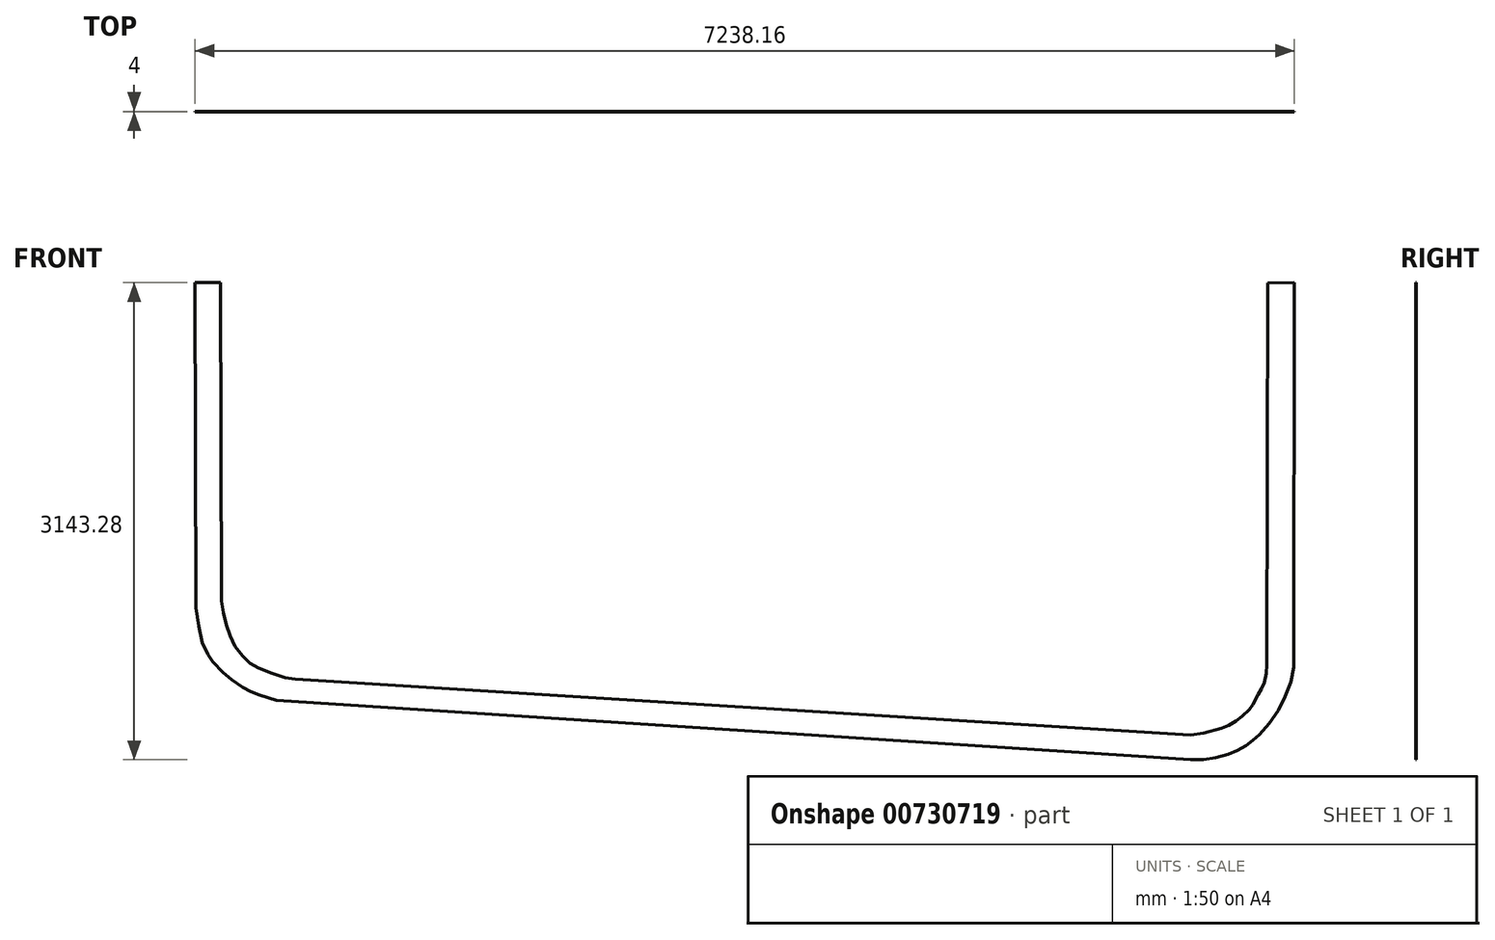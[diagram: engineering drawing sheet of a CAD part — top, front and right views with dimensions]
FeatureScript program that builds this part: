
annotation { "Feature Type Name" : "Feature", "Feature Type Description" : "" }
export const myFeature = defineFeature(function(context is Context, id is Id, definition is map)
    precondition{}
    {
        {
            var Q0;
            Q0=qCreatedBy(makeId("Front.planeOp"),FACE);
            var sketch = newSketch(context, id + "F0", { "sketchPlane" : qUnion([Q0])});
            skLineSegment(sketch, "E0", {"start": v(-3619.08, 1571.64) * mm, "end": v(-3450.88, 1571.64) * mm});
            skLineSegment(sketch, "E1", {"start": v(-3450.88, 1571.64) * mm, "end": v(-3446.72, -525.59) * mm});
            skLineSegment(sketch, "E2", {"start": v(-3446.72, -525.59) * mm, "end": v(-3573.72, -525.84) * mm});
            skLineSegment(sketch, "E3", {"start": v(-3573.72, -525.84) * mm, "end": v(-3446.72, -525.59) * mm});
            skLineSegment(sketch, "E4", {"start": v(-3446.72, -525.59) * mm, "end": v(-3431.83, -603.7) * mm});
            skLineSegment(sketch, "E5", {"start": v(-3431.83, -603.7) * mm, "end": v(-3411.94, -681.16) * mm});
            skLineSegment(sketch, "E6", {"start": v(-3411.94, -681.16) * mm, "end": v(-3389.03, -755.43) * mm});
            skLineSegment(sketch, "E7", {"start": v(-3389.03, -755.43) * mm, "end": v(-3355.94, -824.45) * mm});
            skLineSegment(sketch, "E8", {"start": v(-3355.94, -824.45) * mm, "end": v(-3304.78, -889.17) * mm});
            skLineSegment(sketch, "E9", {"start": v(-3304.78, -889.17) * mm, "end": v(-3259.32, -934.86) * mm});
            skLineSegment(sketch, "E10", {"start": v(-3259.32, -934.86) * mm, "end": v(-3201.02, -968.1) * mm});
            skLineSegment(sketch, "E11", {"start": v(-3201.02, -968.1) * mm, "end": v(-3110.78, -1003.16) * mm});
            skLineSegment(sketch, "E12", {"start": v(-3110.78, -1003.16) * mm, "end": v(-3026.42, -1029.63) * mm});
            skLineSegment(sketch, "E13", {"start": v(-3026.42, -1029.63) * mm, "end": v(-2959.34, -1040.5) * mm});
            skLineSegment(sketch, "E14", {"start": v(-2959.34, -1040.5) * mm, "end": v(-2979.69, -1165.87) * mm});
            skLineSegment(sketch, "E15", {"start": v(-2979.69, -1165.87) * mm, "end": v(-2959.34, -1040.5) * mm});
            skLineSegment(sketch, "E16", {"start": v(-2959.34, -1040.5) * mm, "end": v(2935.08, -1409.53) * mm});
            skLineSegment(sketch, "E17", {"start": v(2935.08, -1409.53) * mm, "end": v(2927.13, -1536.28) * mm});
            skLineSegment(sketch, "E18", {"start": v(2927.13, -1536.28) * mm, "end": v(2935.08, -1409.53) * mm});
            skLineSegment(sketch, "E19", {"start": v(2935.08, -1409.53) * mm, "end": v(3023.48, -1394.9) * mm});
            skLineSegment(sketch, "E20", {"start": v(3023.48, -1394.9) * mm, "end": v(3140.7, -1365.72) * mm});
            skLineSegment(sketch, "E21", {"start": v(3140.7, -1365.72) * mm, "end": v(3188.35, -1344.82) * mm});
            skLineSegment(sketch, "E22", {"start": v(3188.35, -1344.82) * mm, "end": v(3234.63, -1316.42) * mm});
            skLineSegment(sketch, "E23", {"start": v(3234.63, -1316.42) * mm, "end": v(3278.04, -1283.37) * mm});
            skLineSegment(sketch, "E24", {"start": v(3278.04, -1283.37) * mm, "end": v(3323.53, -1240.37) * mm});
            skLineSegment(sketch, "E25", {"start": v(3323.53, -1240.37) * mm, "end": v(3346.54, -1207.58) * mm});
            skLineSegment(sketch, "E26", {"start": v(3346.54, -1207.58) * mm, "end": v(3382.63, -1140.9) * mm});
            skLineSegment(sketch, "E27", {"start": v(3382.63, -1140.9) * mm, "end": v(3403.36, -1102.47) * mm});
            skLineSegment(sketch, "E28", {"start": v(3403.36, -1102.47) * mm, "end": v(3421.16, -1062.9) * mm});
            skLineSegment(sketch, "E29", {"start": v(3421.16, -1062.9) * mm, "end": v(3435.06, -1003.21) * mm});
            skLineSegment(sketch, "E30", {"start": v(3435.06, -1003.21) * mm, "end": v(3437.17, -944.92) * mm});
            skLineSegment(sketch, "E31", {"start": v(3437.17, -944.92) * mm, "end": v(3564.09, -949.52) * mm});
            skLineSegment(sketch, "E32", {"start": v(3564.09, -949.52) * mm, "end": v(3437.17, -944.92) * mm});
            skLineSegment(sketch, "E33", {"start": v(3437.17, -944.92) * mm, "end": v(3444.7, 1569.33) * mm});
            skLineSegment(sketch, "E34", {"start": v(3444.7, 1569.33) * mm, "end": v(3619.08, 1571.64) * mm});
            skLineSegment(sketch, "E35", {"start": v(3619.08, 1571.64) * mm, "end": v(3614.59, -960.51) * mm});
            skLineSegment(sketch, "E36", {"start": v(3614.59, -960.51) * mm, "end": v(3487.59, -960.29) * mm});
            skLineSegment(sketch, "E37", {"start": v(3487.59, -960.29) * mm, "end": v(3614.59, -960.51) * mm});
            skLineSegment(sketch, "E38", {"start": v(3614.59, -960.51) * mm, "end": v(3596.07, -1058.6) * mm});
            skLineSegment(sketch, "E39", {"start": v(3596.07, -1058.6) * mm, "end": v(3559.87, -1153.25) * mm});
            skLineSegment(sketch, "E40", {"start": v(3559.87, -1153.25) * mm, "end": v(3513.9, -1246.57) * mm});
            skLineSegment(sketch, "E41", {"start": v(3513.9, -1246.57) * mm, "end": v(3455.1, -1331) * mm});
            skLineSegment(sketch, "E42", {"start": v(3455.1, -1331) * mm, "end": v(3389.24, -1405.5) * mm});
            skLineSegment(sketch, "E43", {"start": v(3389.24, -1405.5) * mm, "end": v(3347.7, -1443.75) * mm});
            skLineSegment(sketch, "E44", {"start": v(3347.7, -1443.75) * mm, "end": v(3302.72, -1477.91) * mm});
            skLineSegment(sketch, "E45", {"start": v(3302.72, -1477.91) * mm, "end": v(3246.06, -1511.19) * mm});
            skLineSegment(sketch, "E46", {"start": v(3246.06, -1511.19) * mm, "end": v(3185.43, -1536.2) * mm});
            skLineSegment(sketch, "E47", {"start": v(3185.43, -1536.2) * mm, "end": v(3101.05, -1557.19) * mm});
            skLineSegment(sketch, "E48", {"start": v(3101.05, -1557.19) * mm, "end": v(3023.45, -1570.04) * mm});
            skLineSegment(sketch, "E49", {"start": v(3023.45, -1570.04) * mm, "end": v(2937.3, -1571.64) * mm});
            skLineSegment(sketch, "E50", {"start": v(2937.3, -1571.64) * mm, "end": v(2934.9, -1444.66) * mm});
            skLineSegment(sketch, "E51", {"start": v(2934.9, -1444.66) * mm, "end": v(2937.3, -1571.64) * mm});
            skLineSegment(sketch, "E52", {"start": v(2937.3, -1571.64) * mm, "end": v(-3083.83, -1181.32) * mm});
            skLineSegment(sketch, "E53", {"start": v(-3083.83, -1181.32) * mm, "end": v(-3075.62, -1054.6) * mm});
            skLineSegment(sketch, "E54", {"start": v(-3075.62, -1054.6) * mm, "end": v(-3083.83, -1181.32) * mm});
            skLineSegment(sketch, "E55", {"start": v(-3083.83, -1181.32) * mm, "end": v(-3194.65, -1145.48) * mm});
            skLineSegment(sketch, "E56", {"start": v(-3194.65, -1145.48) * mm, "end": v(-3251.8, -1122.34) * mm});
            skLineSegment(sketch, "E57", {"start": v(-3251.8, -1122.34) * mm, "end": v(-3306.38, -1094.17) * mm});
            skLineSegment(sketch, "E58", {"start": v(-3306.38, -1094.17) * mm, "end": v(-3378.72, -1042.4) * mm});
            skLineSegment(sketch, "E59", {"start": v(-3378.72, -1042.4) * mm, "end": v(-3435.26, -995.46) * mm});
            skLineSegment(sketch, "E60", {"start": v(-3435.26, -995.46) * mm, "end": v(-3502.65, -925.61) * mm});
            skLineSegment(sketch, "E61", {"start": v(-3502.65, -925.61) * mm, "end": v(-3533.46, -878.85) * mm});
            skLineSegment(sketch, "E62", {"start": v(-3533.46, -878.85) * mm, "end": v(-3571.56, -797.65) * mm});
            skLineSegment(sketch, "E63", {"start": v(-3571.56, -797.65) * mm, "end": v(-3594.95, -690.49) * mm});
            skLineSegment(sketch, "E64", {"start": v(-3594.95, -690.49) * mm, "end": v(-3612.7, -570.06) * mm});
            skLineSegment(sketch, "E65", {"start": v(-3612.7, -570.06) * mm, "end": v(-3487.05, -551.55) * mm});
            skLineSegment(sketch, "E66", {"start": v(-3487.05, -551.55) * mm, "end": v(-3612.7, -570.06) * mm});
            skLineSegment(sketch, "E67", {"start": v(-3612.7, -570.06) * mm, "end": v(-3619.08, 1571.64) * mm});
            skSolve(sketch);
        }
        {
            var Q0;
            Q0 = qSketchRegion(id + "F0", true);
            extrude(context, id + "F1", {"entities" : qUnion([Q0]), "depth" : 4 * mm, "offsetDistance" : 25 * mm});
        }
    });
